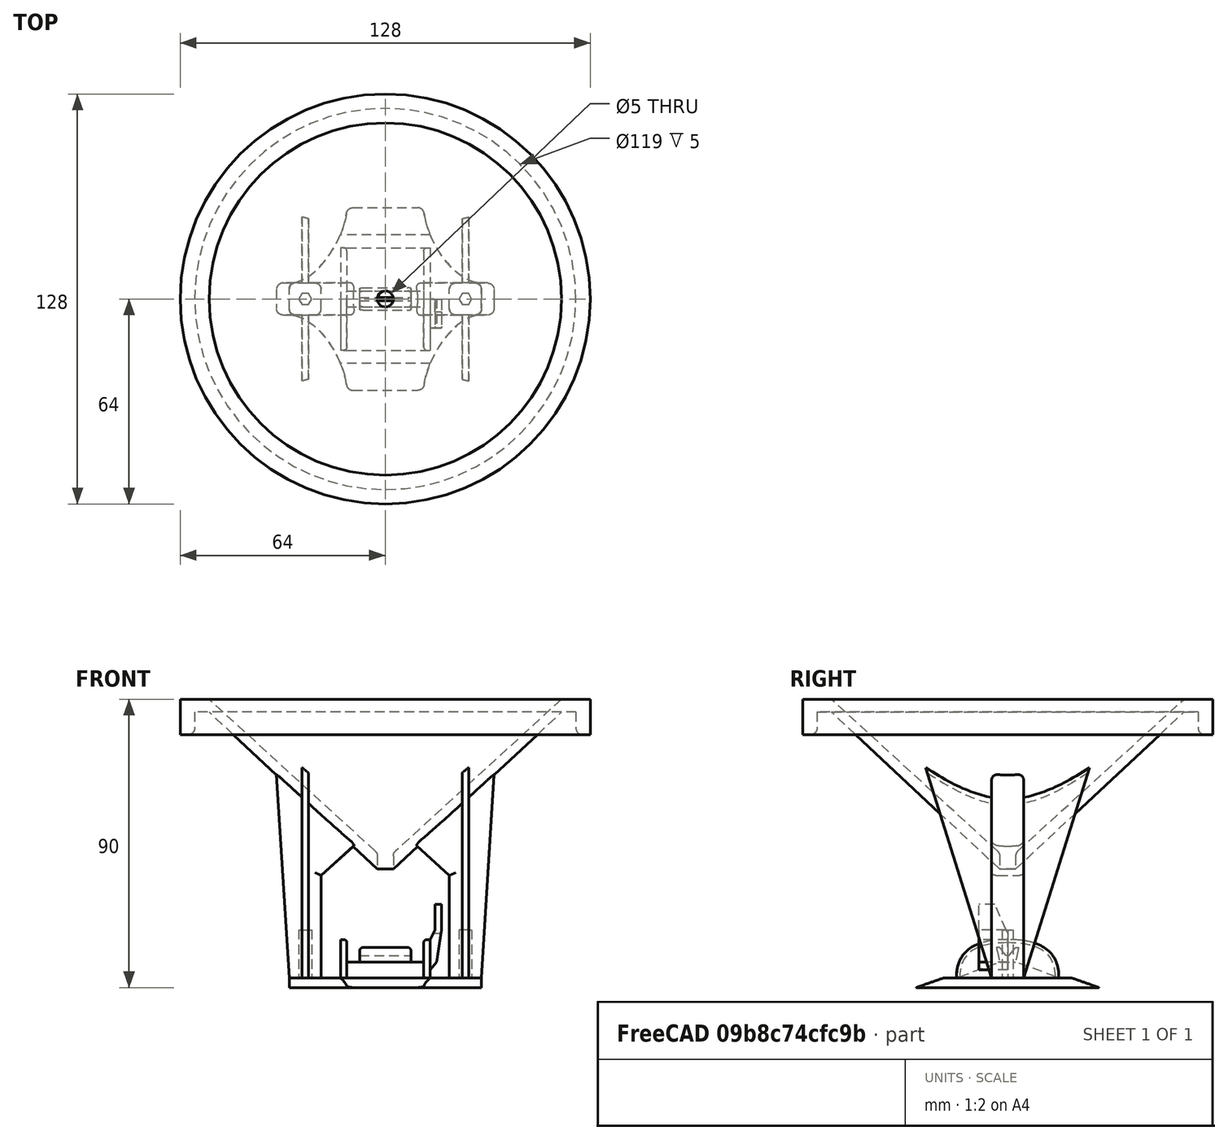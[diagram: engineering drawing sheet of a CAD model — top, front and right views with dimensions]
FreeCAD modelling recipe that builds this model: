
FCSTD DOCUMENT  (FreeCAD 0.19R24267 (Git))
Label: Rain_Gauge_Public_WIP
License: Public Domain
objects: Sketcher::SketchObject×11, PartDesign::Mirrored×10, PartDesign::Pad×7, PartDesign::Pocket×3, PartDesign::Fillet×3, PartDesign::Plane×2, PartDesign::MultiTransform×2, PartDesign::Body×2, Mesh::Feature×1, PartDesign::Revolution×1
note: 55 computed .brp shape members not serialized (recipe doc carries the construction recipe); baked Part::Feature solids carry a one-line shape summary decoded from their .brp

FEATURE [Mesh::Feature] Seesaw
  Placement = pos=(-1.31e-14,-7e-15,-76) rot=(0,0,-1;1.5708rad)
FEATURE [Sketcher::SketchObject] Sketch
  FullyConstrained = false
  MapMode = 5
  Placement = pos=(0,0,0) rot=(1,0,0;1.5708rad)
  Support = -> [XZ_Plane]
  sketch-geometry (8):
    g0: LineSegment StartX=2.5 StartY=53 StartZ=0 EndX=55 EndY=4 EndZ=0
    g1: LineSegment StartX=55 StartY=4 StartZ=0 EndX=59.5 EndY=4 EndZ=0
    g2: LineSegment StartX=59.5 StartY=4 StartZ=0 EndX=59.5 EndY=11 EndZ=0
    g3: LineSegment StartX=59.5 StartY=11 StartZ=0 EndX=64 EndY=11 EndZ=0
    g4: LineSegment StartX=64 StartY=11 StartZ=0 EndX=64 EndY=0 EndZ=0
    g5: LineSegment StartX=64 StartY=0 StartZ=0 EndX=55 EndY=0 EndZ=0
    g6: LineSegment StartX=55 StartY=0 StartZ=0 EndX=2.5 EndY=48 EndZ=0
    g7: LineSegment StartX=2.5 StartY=48 StartZ=0 EndX=2.5 EndY=53 EndZ=0
  constraints (23):
    c: Coincident(g0,g1)
    c: Horizontal(g1)
    c: Coincident(g1,g2)
    c: Vertical(g2)
    c: Coincident(g2,g3)
    c: Horizontal(g3)
    c: Coincident(g3,g4)
    c: Vertical(g4)
    c: Coincident(g4,g5)
    c: Horizontal(g5)
    c: Coincident(g5,g6)
    c: Coincident(g6,g7)
    c: Coincident(g7,g0)
    c: Vertical(g7)
    c: DistanceX(g0) = 2.5
    c: DistanceX(g0) = 55
    c: Vertical(g5,g0)
    c: DistanceY(g5,g0) = 4
    c: DistanceX(g1,g1) = 4.5
    c: DistanceX(g3,g3) = 4.5
    c: DistanceY(g2,g2) = 7
    c: DistanceY(g4,g0) = 53
    c: DistanceY(g7,g7) = 5
FEATURE [PartDesign::Revolution] Revolution
  Angle = 360
  Axis = (0,2e-16,1)
  Base = (0,0,0)
  Placement = pos=(0,0,0) rot=(1,0,0;1.5708rad)
  Profile = -> Sketch
  ReferenceAxis = -> Sketch [V_Axis]
  Refine = true
  Reversed = true
FEATURE [Sketcher::SketchObject] Sketch001
  FullyConstrained = false
  MapMode = 5
  Placement = pos=(0,0,0) rot=(1,0,0;1.5708rad)
  Support = -> [XZ_Plane]
  sketch-geometry (5):
    g0: LineSegment StartX=9 StartY=45 StartZ=0 EndX=20 EndY=55 EndZ=0
    g1: LineSegment StartX=20 StartY=55 StartZ=0 EndX=20 EndY=87 EndZ=0
    g2: LineSegment StartX=20 StartY=87 StartZ=0 EndX=30 EndY=87 EndZ=0
    g3: LineSegment StartX=30 StartY=87 StartZ=0 EndX=34 EndY=23 EndZ=0
    g4: LineSegment StartX=34 StartY=23 StartZ=0 EndX=9 EndY=45 EndZ=0
  constraints (7):
    c: Coincident(g0,g1)
    c: Vertical(g1)
    c: Coincident(g1,g2)
    c: Horizontal(g2)
    c: Coincident(g2,g3)
    c: Coincident(g3,g4)
    c: Coincident(g4,g0)
FEATURE [PartDesign::Pad] Pad
  BaseFeature = -> Revolution
  Direction = (1,1,1)
  Length = 10
  Length2 = 100
  Midplane = true
  Placement = pos=(0,0,0) rot=(1,0,0;1.5708rad)
  Profile = -> Sketch001
  Refine = true
  Type = 0
FEATURE [PartDesign::Mirrored] Mirrored
  BaseFeature = -> Pad
  MirrorPlane = -> Sketch001 [V_Axis]
  Originals = -> [Pad]
  Placement = pos=(0,0,0) rot=(1,0,0;1.5708rad)
  Refine = true
FEATURE [PartDesign::Plane] DatumPlane
  AttachmentOffset = pos=(0,0,72) rot=(0,0,1;0rad)
  Length = 153.539
  MapMode = 5
  Placement = pos=(0,0,72) rot=(0,0,1;0rad)
  ResizeMode = 0
  Support = -> [XY_Plane]
  Width = 153.565
FEATURE [Sketcher::SketchObject] Sketch003
  FullyConstrained = false
  MapMode = 5
  Placement = pos=(0,0,72) rot=(0,0,1;0rad)
  Support = -> [DatumPlane]
  sketch-geometry (7):
    g0: LineSegment StartX=27 StartY=0 StartZ=0 EndX=26 EndY=1.73205 EndZ=0
    g1: LineSegment StartX=26 StartY=1.73205 StartZ=0 EndX=24 EndY=1.73205 EndZ=0
    g2: LineSegment StartX=24 StartY=1.73205 StartZ=0 EndX=23 EndY=2e-16 EndZ=0
    g3: LineSegment StartX=23 StartY=2e-16 StartZ=0 EndX=24 EndY=-1.73205 EndZ=0
    g4: LineSegment StartX=24 StartY=-1.73205 StartZ=0 EndX=26 EndY=-1.73205 EndZ=0
    g5: LineSegment StartX=26 StartY=-1.73205 StartZ=0 EndX=27 EndY=0 EndZ=0
    g6: Circle CenterX=25 CenterY=0 CenterZ=0 NormalX=0 NormalY=0 NormalZ=1 AngleXU=0 Radius=2
  constraints (15):
    c: Coincident(g0,g1)
    c: Coincident(g1,g2)
    c: Coincident(g2,g3)
    c: Coincident(g3,g4)
    c: Coincident(g4,g5)
    c: Coincident(g5,g0)
    c: Equal(g0, g1-g5) x5
    c: PointOnObject(g0,g6)
    c: PointOnObject(g1,g6)
    c: PointOnObject(g2,g6)
    c: PointOnObject(g3,g6)
    c: PointOnObject(g4,g6)
    c: PointOnObject(g5,g6)
    c: PointOnObject(g6,g-1)
    c: PointOnObject(g5,g-1)
FEATURE [PartDesign::Pocket] Pocket
  BaseFeature = -> Mirrored
  Length = 5
  Length2 = 100
  Placement = pos=(0,0,0) rot=(1,0,0;1.5708rad)
  Profile = -> Sketch003
  Refine = true
  Reversed = true
  Type = 1
FEATURE [PartDesign::Mirrored] Mirrored001
  BaseFeature = -> Pocket
  MirrorPlane = -> Sketch003 [V_Axis]
  Originals = -> [Pocket]
  Placement = pos=(0,0,0) rot=(1,0,0;1.5708rad)
  Refine = true
FEATURE [PartDesign::Plane] DatumPlane001
  AttachmentOffset = pos=(0,0,-25) rot=(0,0,1;0rad)
  Length = 151.918
  MapMode = 5
  Placement = pos=(-25,5.6e-15,-5.6e-15) rot=(0.57735,0.57735,0.57735;2.0944rad)
  ResizeMode = 0
  Support = -> [YZ_Plane]
  Width = 135.944
FEATURE [Sketcher::SketchObject] Sketch004
  FullyConstrained = false
  MapMode = 5
  Placement = pos=(-25,5.6e-15,-5.6e-15) rot=(0.57735,0.57735,0.57735;2.0944rad)
  Support = -> [DatumPlane001]
  sketch-geometry (4):
    g0: LineSegment StartX=5 StartY=87 StartZ=0 EndX=26 EndY=20 EndZ=0
    g1: LineSegment StartX=26 StartY=20 StartZ=0 EndX=4 EndY=30 EndZ=0
    g2: LineSegment StartX=4 StartY=30 StartZ=0 EndX=4 EndY=86 EndZ=0
    g3: LineSegment StartX=4 StartY=86 StartZ=0 EndX=5 EndY=87 EndZ=0
  constraints (5):
    c: Coincident(g0,g1)
    c: Coincident(g1,g2)
    c: Vertical(g2)
    c: Coincident(g2,g3)
    c: Coincident(g3,g0)
FEATURE [PartDesign::Pad] Pad001
  BaseFeature = -> Mirrored001
  Direction = (1,1,1)
  Length = 2
  Length2 = 100
  Midplane = true
  Placement = pos=(0,0,0) rot=(1,0,0;1.5708rad)
  Profile = -> Sketch004
  Refine = true
  Type = 0
FEATURE [PartDesign::Mirrored] Mirrored002
  MirrorPlane = -> XZ_Plane
  Placement = pos=(0,0,0) rot=(1,0,0;1.5708rad)
  Refine = true
FEATURE [PartDesign::Mirrored] Mirrored003
  MirrorPlane = -> YZ_Plane
  Placement = pos=(0,0,0) rot=(1,0,0;1.5708rad)
  Refine = true
FEATURE [PartDesign::MultiTransform] MultiTransform
  BaseFeature = -> Pad001
  Originals = -> [Pad001]
  Placement = pos=(0,0,0) rot=(1,0,0;1.5708rad)
  Refine = true
  Transformations = -> [Mirrored002,Mirrored003]
FEATURE [PartDesign::Fillet] Fillet
  Base = -> MultiTransform [Edge73,Edge75,Edge43,Edge45,Edge64,Edge61,Edge58,Edge35,Edge38,Edge31,Edge87,Edge55,Edge33,Edge56]
  BaseFeature = -> MultiTransform
  Placement = pos=(0,0,0) rot=(1,0,0;1.5708rad)
  Radius = 2
  Refine = true
  SupportTransform = true
FEATURE [PartDesign::Body] Body  label="Funnel"
  Group = -> [DatumPlane,Sketch,Revolution,Sketch001,Pad,Mirrored,Sketch003,Pocket,Mirrored001,DatumPlane001,Sketch004,Pad001,MultiTransform,Mirrored002,Mirrored003,Fillet]
  Origin = -> Origin
  Placement = pos=(0,0,0) rot=(1,0,0;3.14159rad)
  Tip = -> Fillet
FEATURE [Sketcher::SketchObject] Sketch005
  AttachmentOffset = pos=(0,0,87) rot=(0,0,1;0rad)
  FullyConstrained = false
  MapMode = 5
  Placement = pos=(0,0,87) rot=(0,0,1;0rad)
  Support = -> [XY_Plane001]
  sketch-geometry (11):
    g0: LineSegment StartX=-12 StartY=28.5 StartZ=0 EndX=0 EndY=28.5 EndZ=0
    g1: LineSegment StartX=0 StartY=28.5 StartZ=0 EndX=0 EndY=0 EndZ=0
    g2: LineSegment StartX=0 StartY=0 StartZ=0 EndX=-30 EndY=0 EndZ=0
    g3: LineSegment StartX=-30 StartY=0 StartZ=0 EndX=-30 EndY=5 EndZ=0
    g4-g7: Circle x4 (B-spline internal-alignment scaffolding for g8; pole/knot coordinates omitted)
    g8: BSplineCurve PolesCount=4 KnotsCount=2 Degree=3 IsPeriodic=0
    g9: GeomPoint X=-30 Y=5 Z=0
    g10: GeomPoint X=-12 Y=28.5 Z=0
  constraints (18):
    c: PointOnObject(g0,g-2)
    c: Horizontal(g0)
    c: Coincident(g0,g1)
    c: Coincident(g1,g-1)
    c: Coincident(g1,g2)
    c: PointOnObject(g2,g-1)
    c: Coincident(g2,g3)
    c: Vertical(g3)
    c: DistanceY(g0) = 28.5
    c: Coincident(g8,g3)
    c: Weight(g4) = 1
    c: Equal(g4,g5)
    c: Equal(g4,g6)
    c: Equal(g4,g7)
    c: Coincident(g8,g0)
    c: InternalAlignment(g4-g7 -> g8) x4
    c: InternalAlignment(g9,g8)
    c: InternalAlignment(g10,g8)
FEATURE [PartDesign::Pad] Pad002
  Direction = (1,1,1)
  Length = 3
  Length2 = 100
  Profile = -> Sketch005
  Refine = true
  Type = 0
FEATURE [PartDesign::Mirrored] Mirrored004
  MirrorPlane = -> Sketch005 [H_Axis]
  Refine = true
FEATURE [PartDesign::Mirrored] Mirrored005
  MirrorPlane = -> YZ_Plane001
  Refine = true
FEATURE [PartDesign::Fillet] Fillet001
  Base = -> Pad002 [Edge11,Edge1]
  BaseFeature = -> Pad002
  Radius = 2
  Refine = true
  SupportTransform = true
FEATURE [PartDesign::MultiTransform] MultiTransform001
  BaseFeature = -> Fillet001
  Originals = -> [Fillet001]
  Refine = true
  Transformations = -> [Mirrored004,Mirrored005]
FEATURE [Sketcher::SketchObject] Sketch006
  FullyConstrained = false
  MapMode = 5
  Placement = pos=(0,0,0) rot=(0.57735,0.57735,0.57735;2.0944rad)
  Support = -> [YZ_Plane]
  sketch-geometry (3):
    g0: LineSegment StartX=-31.3668 StartY=91 StartZ=0 EndX=-17.2145 EndY=86 EndZ=0
    g1: LineSegment StartX=-17.2145 StartY=86 StartZ=0 EndX=-31.3668 EndY=86 EndZ=0
    g2: LineSegment StartX=-31.3668 StartY=86 StartZ=0 EndX=-31.3668 EndY=91 EndZ=0
  constraints (5):
    c: Coincident(g0,g1)
    c: Horizontal(g1)
    c: Coincident(g1,g2)
    c: Coincident(g2,g0)
    c: Vertical(g2)
FEATURE [PartDesign::Pocket] Pocket001
  BaseFeature = -> MultiTransform001
  Length = 5
  Length2 = 100
  Midplane = true
  Profile = -> Sketch006
  Refine = true
  Type = 1
FEATURE [PartDesign::Mirrored] Mirrored006
  BaseFeature = -> Pocket001
  MirrorPlane = -> Sketch006 [V_Axis]
  Originals = -> [Pocket001]
  Refine = true
FEATURE [Sketcher::SketchObject] Sketch007
  AttachmentOffset = pos=(0,0,12) rot=(0,0,1;0rad)
  FullyConstrained = false
  MapMode = 5
  Placement = pos=(12,-2.7e-15,2.7e-15) rot=(0.57735,0.57735,0.57735;2.0944rad)
  Support = -> [YZ_Plane001]
  sketch-geometry (15):
    g0-g3: Circle x4 (B-spline internal-alignment scaffolding for g4; pole/knot coordinates omitted)
    g4: BSplineCurve PolesCount=4 KnotsCount=2 Degree=3 IsPeriodic=0
    g5: GeomPoint X=-16 Y=87 Z=0
    g6: GeomPoint X=0 Y=75 Z=0
    g7-g10: Circle x4 (B-spline internal-alignment scaffolding for g11; pole/knot coordinates omitted)
    g11: BSplineCurve PolesCount=4 KnotsCount=2 Degree=3 IsPeriodic=0
    g12: GeomPoint X=0 Y=75 Z=0
    g13: GeomPoint X=16 Y=87 Z=0
    g14: LineSegment StartX=-16 StartY=87 StartZ=0 EndX=16 EndY=87 EndZ=0
  constraints (19):
    c: Weight(g0) = 1
    c: Equal(g0,g1)
    c: Equal(g0,g2)
    c: Equal(g0,g3)
    c: PointOnObject(g4,g-2)
    c: InternalAlignment(g0-g3 -> g4) x4
    c: InternalAlignment(g5,g4)
    c: InternalAlignment(g6,g4)
    c: Coincident(g11,g4)
    c: Weight(g7) = 1
    c: Equal(g7,g8)
    c: Equal(g7,g9)
    c: Equal(g7,g10)
    c: InternalAlignment(g7-g10 -> g11) x4
    c: InternalAlignment(g12,g11)
    c: InternalAlignment(g13,g11)
    c: Coincident(g14,g4)
    c: Coincident(g14,g11)
    c: Horizontal(g14)
FEATURE [PartDesign::Pad] Pad003
  BaseFeature = -> Mirrored006
  Direction = (1,1,1)
  Length = 2
  Length2 = 100
  Profile = -> Sketch007
  Refine = true
  Type = 0
FEATURE [PartDesign::Mirrored] Mirrored007
  BaseFeature = -> Pad003
  MirrorPlane = -> YZ_Plane001
  Originals = -> [Pad003]
  Refine = true
FEATURE [Sketcher::SketchObject] Sketch008
  FullyConstrained = false
  MapMode = 5
  Placement = pos=(0,0,0) rot=(0.57735,0.57735,0.57735;2.0944rad)
  Support = -> [YZ_Plane001]
  sketch-geometry (4):
    g0: LineSegment StartX=-16 StartY=87 StartZ=0 EndX=-2.49693 EndY=82 EndZ=0
    g1: LineSegment StartX=-2.49693 StartY=82 StartZ=0 EndX=0 EndY=82 EndZ=0
    g2: LineSegment StartX=0 StartY=82 StartZ=0 EndX=0 EndY=87 EndZ=0
    g3: LineSegment StartX=0 StartY=87 StartZ=0 EndX=-16 EndY=87 EndZ=0
  constraints (8):
    c: PointOnObject(g1,g-2)
    c: Horizontal(g1)
    c: Coincident(g1,g2)
    c: PointOnObject(g2,g-2)
    c: Coincident(g2,g3)
    c: Coincident(g3,g0)
    c: Horizontal(g3)
    c: Coincident(g0,g1)
FEATURE [PartDesign::Pad] Pad004
  BaseFeature = -> Mirrored007
  Direction = (1,1,1)
  Length = 24
  Length2 = 100
  Midplane = true
  Profile = -> Sketch008
  Refine = true
  Type = 0
FEATURE [PartDesign::Mirrored] Mirrored008
  BaseFeature = -> Pad004
  MirrorPlane = -> Sketch008 [V_Axis]
  Originals = -> [Pad004]
  Refine = true
FEATURE [Sketcher::SketchObject] Sketch009
  FullyConstrained = false
  MapMode = 5
  Placement = pos=(0,0,0) rot=(0.57735,0.57735,0.57735;2.0944rad)
  Support = -> [YZ_Plane001]
  sketch-geometry (6):
    g0: LineSegment StartX=-3.49822 StartY=77.4972 StartZ=0 EndX=-2.50597 EndY=82 EndZ=0
    g1: LineSegment StartX=-2.50597 StartY=82 StartZ=0 EndX=0 EndY=82 EndZ=0
    g2: LineSegment StartX=0 StartY=82 StartZ=0 EndX=0 EndY=80 EndZ=0
    g3: LineSegment StartX=0 StartY=80 StartZ=0 EndX=-0.489203 EndY=80 EndZ=0
    g4: LineSegment StartX=-0.489203 StartY=80 StartZ=0 EndX=-2.50372 EndY=77.4972 EndZ=0
    g5: LineSegment StartX=-2.50372 StartY=77.4972 StartZ=0 EndX=-3.49822 EndY=77.4972 EndZ=0
  constraints (10):
    c: Coincident(g0,g1)
    c: Horizontal(g1)
    c: Coincident(g1,g2)
    c: Vertical(g2)
    c: Coincident(g2,g3)
    c: Horizontal(g3)
    c: Coincident(g3,g4)
    c: Coincident(g4,g5)
    c: Coincident(g5,g0)
    c: Horizontal(g5)
FEATURE [PartDesign::Pad] Pad005
  BaseFeature = -> Mirrored008
  Direction = (1,1,1)
  Length = 16
  Length2 = 100
  Midplane = true
  Profile = -> Sketch009
  Refine = true
  Type = 0
FEATURE [PartDesign::Mirrored] Mirrored009
  BaseFeature = -> Pad005
  MirrorPlane = -> Sketch009 [V_Axis]
  Originals = -> [Pad005]
  Refine = true
FEATURE [Sketcher::SketchObject] Sketch010
  FullyConstrained = false
  MapMode = 5
  Placement = pos=(0,0,0) rot=(1,0,0;1.5708rad)
  Support = -> [XZ_Plane001]
  sketch-geometry (7):
    g0: LineSegment StartX=14 StartY=84.5115 StartZ=0 EndX=16 EndY=82 EndZ=0
    g1: LineSegment StartX=16 StartY=82 StartZ=0 EndX=17.5192 EndY=72 EndZ=0
    g2: LineSegment StartX=17.5192 StartY=72 StartZ=0 EndX=17.5192 EndY=64 EndZ=0
    g3: LineSegment StartX=17.5192 StartY=64 StartZ=0 EndX=15.5126 EndY=64 EndZ=0
    g4: LineSegment StartX=15.5126 StartY=64 StartZ=0 EndX=15.5126 EndY=72 EndZ=0
    g5: LineSegment StartX=15.5126 StartY=72 StartZ=0 EndX=14 EndY=75 EndZ=0
    g6: LineSegment StartX=14 StartY=75 StartZ=0 EndX=14 EndY=84.5115 EndZ=0
  constraints (11):
    c: Coincident(g0,g1)
    c: Coincident(g1,g2)
    c: Vertical(g2)
    c: Coincident(g2,g3)
    c: Horizontal(g3)
    c: Coincident(g3,g4)
    c: Vertical(g4)
    c: Coincident(g4,g5)
    c: Coincident(g5,g6)
    c: Coincident(g6,g0)
    c: Vertical(g6)
FEATURE [PartDesign::Pad] Pad006
  BaseFeature = -> Mirrored009
  Direction = (1,1,1)
  Length = 9
  Length2 = 100
  Profile = -> Sketch010
  Refine = true
  Reversed = true
  Type = 0
FEATURE [Sketcher::SketchObject] Sketch011
  FullyConstrained = false
  MapMode = 5
  Placement = pos=(0,0,0) rot=(0.57735,0.57735,0.57735;2.0944rad)
  Support = -> [YZ_Plane001]
  sketch-geometry (3):
    g0: LineSegment StartX=0 StartY=73 StartZ=0 EndX=4 EndY=64 EndZ=0
    g1: LineSegment StartX=4 StartY=64 StartZ=0 EndX=0 EndY=64 EndZ=0
    g2: LineSegment StartX=0 StartY=64 StartZ=0 EndX=0 EndY=73 EndZ=0
  constraints (6):
    c: PointOnObject(g0,g-2)
    c: Coincident(g0,g1)
    c: PointOnObject(g1,g-2)
    c: Horizontal(g1)
    c: Coincident(g1,g2)
    c: Coincident(g2,g0)
FEATURE [PartDesign::Pocket] Pocket002
  BaseFeature = -> Pad006
  Length = 5
  Length2 = 100
  Profile = -> Sketch011
  Refine = true
  Reversed = true
  Type = 1
FEATURE [PartDesign::Fillet] Fillet002
  Base = -> Pocket002 [Edge10,Edge23,Edge17,Edge9,Edge42,Edge46]
  BaseFeature = -> Pocket002
  Radius = 1
  Refine = true
  SupportTransform = true
FEATURE [PartDesign::Body] Body001  label="Baseplate001"
  Group = -> [Sketch005,Pad002,Fillet001,MultiTransform001,Mirrored004,Mirrored005,Sketch006,Pocket001,Mirrored006,Sketch007,Pad003,Mirrored007,Sketch008,Pad004,Mirrored008,Sketch009,Pad005,Mirrored009,Sketch010,Pad006,Sketch011,Pocket002,Fillet002]
  Origin = -> Origin001
  Placement = pos=(0,0,0) rot=(1,0,0;3.14159rad)
  Tip = -> Fillet002
